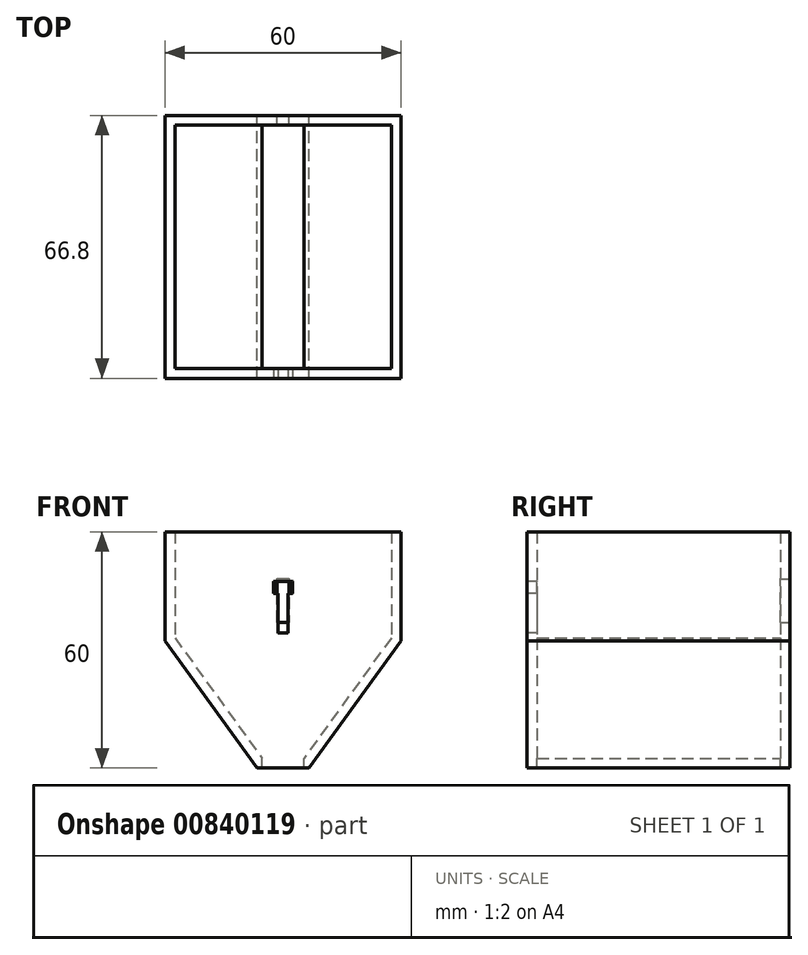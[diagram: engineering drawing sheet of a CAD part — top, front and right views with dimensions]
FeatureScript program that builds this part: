
annotation { "Feature Type Name" : "Feature", "Feature Type Description" : "" }
export const myFeature = defineFeature(function(context is Context, id is Id, definition is map)
    precondition{}
    {
        {
            var Q0;
            Q0=qCreatedBy(makeId("Front.planeOp"),FACE);
            var sketch = newSketch(context, id + "F0", { "sketchPlane" : qUnion([Q0])});
            skLineSegment(sketch, "E0", {"start": v(0, 4.02) * mm, "end": v(-30, 4.02) * mm});
            skLineSegment(sketch, "E1", {"start": v(-30, 4.02) * mm, "end": v(-30, -23.74) * mm});
            skLineSegment(sketch, "E2", {"start": v(-30, -23.74) * mm, "end": v(-6.6, -55.98) * mm});
            skLineSegment(sketch, "E3", {"start": v(-6.6, -55.98) * mm, "end": v(0, -55.98) * mm});
            skLineSegment(sketch, "E4", {"start": v(0, 4.02) * mm, "end": v(0, -55.98) * mm});
            skLineSegment(sketch, "E5.MirrorCS", {"start": v(0, 4.02) * mm, "end": v(30, 4.02) * mm});
            skLineSegment(sketch, "E6.MirrorCS", {"start": v(30, 4.02) * mm, "end": v(30, -23.74) * mm});
            skLineSegment(sketch, "E7.MirrorCS", {"start": v(30, -23.74) * mm, "end": v(6.6, -55.98) * mm});
            skLineSegment(sketch, "E8.MirrorCS", {"start": v(6.6, -55.98) * mm, "end": v(0, -55.98) * mm});
            skSolve(sketch);
        }
        {
            var Q0;
            Q0=makeQuery(id+"F0.imprint","IMPRINT",FACE,{"disambiguationData":[TD([[makeQuery(id+"F0.imprint","IMPRINT",EDGE,{"derivedFrom":sQuery(id+"F0.wireOp",EDGE,"E0")}),1.0]])]});
            var Q1;
            Q1=makeQuery(id+"F0.imprint","IMPRINT",FACE,{"disambiguationData":[TD([[makeQuery(id+"F0.imprint","IMPRINT",EDGE,{"derivedFrom":sQuery(id+"F0.wireOp",EDGE,"E4")}),1.0]])]});
            extrude(context, id + "F1", {"entities" : qUnion([Q0, Q1]), "depth" : 66.8 * mm, "offsetDistance" : 25 * mm});
        }
        {
            var Q0;
            Q0=makeQuery(id+"F1.opExtrude","SWEPT_FACE",FACE,{"disambiguationData":[OSD([sQuery(id+"F0.wireOp",EDGE,"E0"),sQuery(id+"F0.wireOp",EDGE,"E5.MirrorCS")])]});
            shell(context, id + "F2", {"entities" : qUnion([Q0]), "thickness" : 2.5 * mm});
        }
        {
            var Q0;
            Q0=makeQuery(id+"F2.opShell","OFFSET_FACE",FACE,{"disambiguationData":[OSD([sQuery(id+"F0.wireOp",EDGE,"E3"),sQuery(id+"F0.wireOp",EDGE,"E8.MirrorCS")])]});
            extrude(context, id + "F3", {"entities" : qUnion([Q0]), "operationType" : NewBodyOperationType.REMOVE, "oppositeDirection" : true, "depth" : 25 * mm, "offsetDistance" : 25 * mm});
        }
        {
            var Q0;
            Q0=makeQuery(id+"F1.opExtrude","CAP_FACE",FACE,{"disambiguationData":[OSD([sQuery(id+"F0.wireOp",EDGE,"E0"),sQuery(id+"F0.wireOp",EDGE,"E1"),sQuery(id+"F0.wireOp",EDGE,"E2"),sQuery(id+"F0.wireOp",EDGE,"E3"),sQuery(id+"F0.wireOp",EDGE,"E5.MirrorCS"),sQuery(id+"F0.wireOp",EDGE,"E6.MirrorCS"),sQuery(id+"F0.wireOp",EDGE,"E7.MirrorCS"),sQuery(id+"F0.wireOp",EDGE,"E8.MirrorCS")])],"isStart":false});
            var sketch = newSketch(context, id + "F4", { "sketchPlane" : qUnion([Q0])});
            skLineSegment(sketch, "E9", {"start": v(-2.4, -11.6) * mm, "end": v(-1.25, -11.6) * mm});
            skLineSegment(sketch, "E10", {"start": v(-1.25, -11.6) * mm, "end": v(-1.25, -21.6) * mm});
            skLineSegment(sketch, "E11", {"start": v(-1.25, -21.6) * mm, "end": v(0, -21.6) * mm});
            skLineSegment(sketch, "E12", {"start": v(-2.4, -11.6) * mm, "end": v(-2.4, -8.6) * mm});
            skLineSegment(sketch, "E13", {"start": v(-2.4, -8.6) * mm, "end": v(0, -8.6) * mm});
            skLineSegment(sketch, "E14", {"start": v(0, -8.6) * mm, "end": v(0, -21.6) * mm});
            skLineSegment(sketch, "E15.MirrorCS", {"start": v(2.4, -8.6) * mm, "end": v(0, -8.6) * mm});
            skLineSegment(sketch, "E16.MirrorCS", {"start": v(2.4, -11.6) * mm, "end": v(2.4, -8.6) * mm});
            skLineSegment(sketch, "E17.MirrorCS", {"start": v(2.4, -11.6) * mm, "end": v(1.25, -11.6) * mm});
            skLineSegment(sketch, "E18.MirrorCS", {"start": v(1.25, -11.6) * mm, "end": v(1.25, -21.6) * mm});
            skLineSegment(sketch, "E19.MirrorCS", {"start": v(1.25, -21.6) * mm, "end": v(0, -21.6) * mm});
            skSolve(sketch);
        }
        {
            var Q0;
            Q0=makeQuery(id+"F4.imprint","IMPRINT",FACE,{"disambiguationData":[TD([[makeQuery(id+"F4.imprint","IMPRINT",EDGE,{"derivedFrom":sQuery(id+"F4.wireOp",EDGE,"E9")}),1.0]])]});
            var Q1;
            Q1=makeQuery(id+"F4.imprint","IMPRINT",FACE,{"disambiguationData":[TD([[makeQuery(id+"F4.imprint","IMPRINT",EDGE,{"derivedFrom":sQuery(id+"F4.wireOp",EDGE,"E14")}),1.0]])]});
            extrude(context, id + "F5", {"entities" : qUnion([Q0, Q1]), "operationType" : NewBodyOperationType.REMOVE, "oppositeDirection" : true, "depth" : 25 * mm, "offsetDistance" : 25 * mm});
        }
        {
            var Q0;
            Q0=makeQuery(id+"F5.boolean.opBoolean","COPY",EDGE,{"derivedFrom":makeQuery(id+"F5.opExtrude","SWEPT_EDGE",EDGE,{"disambiguationData":[OSD([sQuery(id+"F4.wireOp",EDGE,"E17.MirrorCS"),sQuery(id+"F4.wireOp",EDGE,"E18.MirrorCS")])]})});
            var Q1;
            Q1=makeQuery(id+"F5.boolean.opBoolean","COPY",EDGE,{"derivedFrom":makeQuery(id+"F5.opExtrude","SWEPT_EDGE",EDGE,{"disambiguationData":[OSD([sQuery(id+"F4.wireOp",EDGE,"E9"),sQuery(id+"F4.wireOp",EDGE,"E10")])]})});
            var Q2;
            {var subQ0=sQuery(id+"F0.wireOp",EDGE,"E8.MirrorCS");var subQ1=sQuery(id+"F0.wireOp",EDGE,"E3");var subQ2=sQuery(id+"F0.wireOp",EDGE,"E7.MirrorCS");var subQ3=sQuery(id+"F0.wireOp",EDGE,"E6.MirrorCS");var subQ4=sQuery(id+"F0.wireOp",EDGE,"E5.MirrorCS");var subQ5=sQuery(id+"F0.wireOp",EDGE,"E2");var subQ6=sQuery(id+"F0.wireOp",EDGE,"E1");var subQ7=sQuery(id+"F0.wireOp",EDGE,"E0");Q2=makeQuery(id+"F5.boolean.opBoolean","INTERSECT",EDGE,{"derivedFrom":[makeQuery(id+"F3.boolean.opBoolean","MERGE",FACE,{"derivedFrom":[makeQuery(id+"F2.opShell","OFFSET_FACE",FACE,{"disambiguationData":[OSD([subQ7,subQ6,subQ5,subQ1,subQ4,subQ3,subQ2,subQ0]),TDD([makeQuery(id+"F1.opExtrude","CAP_FACE",FACE,{"disambiguationData":[OSD([subQ7,subQ6,subQ5,subQ1,subQ4,subQ3,subQ2,subQ0])],"isStart":false})])]}),makeQuery(id+"F3.opExtrude","SWEPT_FACE",FACE,{"disambiguationData":[OSD([subQ1,subQ0]),TDD([makeQuery(id+"F2.opShell","OFFSET_EDGE",EDGE,{"disambiguationData":[OSD([subQ1,subQ0]),TDD([makeQuery(id+"F1.opExtrude","CAP_EDGE",EDGE,{"disambiguationData":[OSD([subQ1,subQ0])],"isStart":false})])]})])]})]}),makeQuery(id+"F5.opExtrude","SWEPT_FACE",FACE,{"disambiguationData":[OSD([sQuery(id+"F4.wireOp",EDGE,"E13"),sQuery(id+"F4.wireOp",EDGE,"E15.MirrorCS")])]})]});}
            var Q3;
            {var subQ0=sQuery(id+"F0.wireOp",EDGE,"E8.MirrorCS");var subQ1=sQuery(id+"F0.wireOp",EDGE,"E3");var subQ2=sQuery(id+"F0.wireOp",EDGE,"E7.MirrorCS");var subQ3=sQuery(id+"F0.wireOp",EDGE,"E6.MirrorCS");var subQ4=sQuery(id+"F0.wireOp",EDGE,"E5.MirrorCS");var subQ5=sQuery(id+"F0.wireOp",EDGE,"E2");var subQ6=sQuery(id+"F0.wireOp",EDGE,"E1");var subQ7=sQuery(id+"F0.wireOp",EDGE,"E0");Q3=makeQuery(id+"F5.boolean.opBoolean","INTERSECT",EDGE,{"derivedFrom":[makeQuery(id+"F3.boolean.opBoolean","MERGE",FACE,{"derivedFrom":[makeQuery(id+"F2.opShell","OFFSET_FACE",FACE,{"disambiguationData":[OSD([subQ7,subQ6,subQ5,subQ1,subQ4,subQ3,subQ2,subQ0]),TDD([makeQuery(id+"F1.opExtrude","CAP_FACE",FACE,{"disambiguationData":[OSD([subQ7,subQ6,subQ5,subQ1,subQ4,subQ3,subQ2,subQ0])],"isStart":false})])]}),makeQuery(id+"F3.opExtrude","SWEPT_FACE",FACE,{"disambiguationData":[OSD([subQ1,subQ0]),TDD([makeQuery(id+"F2.opShell","OFFSET_EDGE",EDGE,{"disambiguationData":[OSD([subQ1,subQ0]),TDD([makeQuery(id+"F1.opExtrude","CAP_EDGE",EDGE,{"disambiguationData":[OSD([subQ1,subQ0])],"isStart":false})])]})])]})]}),makeQuery(id+"F5.opExtrude","SWEPT_FACE",FACE,{"disambiguationData":[OSD([sQuery(id+"F4.wireOp",EDGE,"E16.MirrorCS")])]})]});}
            var Q4;
            {var subQ0=sQuery(id+"F0.wireOp",EDGE,"E8.MirrorCS");var subQ1=sQuery(id+"F0.wireOp",EDGE,"E3");var subQ2=sQuery(id+"F0.wireOp",EDGE,"E7.MirrorCS");var subQ3=sQuery(id+"F0.wireOp",EDGE,"E6.MirrorCS");var subQ4=sQuery(id+"F0.wireOp",EDGE,"E5.MirrorCS");var subQ5=sQuery(id+"F0.wireOp",EDGE,"E2");var subQ6=sQuery(id+"F0.wireOp",EDGE,"E1");var subQ7=sQuery(id+"F0.wireOp",EDGE,"E0");Q4=makeQuery(id+"F5.boolean.opBoolean","INTERSECT",EDGE,{"derivedFrom":[makeQuery(id+"F3.boolean.opBoolean","MERGE",FACE,{"derivedFrom":[makeQuery(id+"F2.opShell","OFFSET_FACE",FACE,{"disambiguationData":[OSD([subQ7,subQ6,subQ5,subQ1,subQ4,subQ3,subQ2,subQ0]),TDD([makeQuery(id+"F1.opExtrude","CAP_FACE",FACE,{"disambiguationData":[OSD([subQ7,subQ6,subQ5,subQ1,subQ4,subQ3,subQ2,subQ0])],"isStart":false})])]}),makeQuery(id+"F3.opExtrude","SWEPT_FACE",FACE,{"disambiguationData":[OSD([subQ1,subQ0]),TDD([makeQuery(id+"F2.opShell","OFFSET_EDGE",EDGE,{"disambiguationData":[OSD([subQ1,subQ0]),TDD([makeQuery(id+"F1.opExtrude","CAP_EDGE",EDGE,{"disambiguationData":[OSD([subQ1,subQ0])],"isStart":false})])]})])]})]}),makeQuery(id+"F5.opExtrude","SWEPT_FACE",FACE,{"disambiguationData":[OSD([sQuery(id+"F4.wireOp",EDGE,"E17.MirrorCS")])]})]});}
            var Q5;
            {var subQ0=sQuery(id+"F0.wireOp",EDGE,"E8.MirrorCS");var subQ1=sQuery(id+"F0.wireOp",EDGE,"E3");var subQ2=sQuery(id+"F0.wireOp",EDGE,"E7.MirrorCS");var subQ3=sQuery(id+"F0.wireOp",EDGE,"E6.MirrorCS");var subQ4=sQuery(id+"F0.wireOp",EDGE,"E5.MirrorCS");var subQ5=sQuery(id+"F0.wireOp",EDGE,"E2");var subQ6=sQuery(id+"F0.wireOp",EDGE,"E1");var subQ7=sQuery(id+"F0.wireOp",EDGE,"E0");Q5=makeQuery(id+"F5.boolean.opBoolean","INTERSECT",EDGE,{"derivedFrom":[makeQuery(id+"F3.boolean.opBoolean","MERGE",FACE,{"derivedFrom":[makeQuery(id+"F2.opShell","OFFSET_FACE",FACE,{"disambiguationData":[OSD([subQ7,subQ6,subQ5,subQ1,subQ4,subQ3,subQ2,subQ0]),TDD([makeQuery(id+"F1.opExtrude","CAP_FACE",FACE,{"disambiguationData":[OSD([subQ7,subQ6,subQ5,subQ1,subQ4,subQ3,subQ2,subQ0])],"isStart":false})])]}),makeQuery(id+"F3.opExtrude","SWEPT_FACE",FACE,{"disambiguationData":[OSD([subQ1,subQ0]),TDD([makeQuery(id+"F2.opShell","OFFSET_EDGE",EDGE,{"disambiguationData":[OSD([subQ1,subQ0]),TDD([makeQuery(id+"F1.opExtrude","CAP_EDGE",EDGE,{"disambiguationData":[OSD([subQ1,subQ0])],"isStart":false})])]})])]})]}),makeQuery(id+"F5.opExtrude","SWEPT_FACE",FACE,{"disambiguationData":[OSD([sQuery(id+"F4.wireOp",EDGE,"E18.MirrorCS")])]})]});}
            var Q6;
            {var subQ0=sQuery(id+"F0.wireOp",EDGE,"E8.MirrorCS");var subQ1=sQuery(id+"F0.wireOp",EDGE,"E3");var subQ2=sQuery(id+"F0.wireOp",EDGE,"E7.MirrorCS");var subQ3=sQuery(id+"F0.wireOp",EDGE,"E6.MirrorCS");var subQ4=sQuery(id+"F0.wireOp",EDGE,"E5.MirrorCS");var subQ5=sQuery(id+"F0.wireOp",EDGE,"E2");var subQ6=sQuery(id+"F0.wireOp",EDGE,"E1");var subQ7=sQuery(id+"F0.wireOp",EDGE,"E0");Q6=makeQuery(id+"F5.boolean.opBoolean","INTERSECT",EDGE,{"derivedFrom":[makeQuery(id+"F3.boolean.opBoolean","MERGE",FACE,{"derivedFrom":[makeQuery(id+"F2.opShell","OFFSET_FACE",FACE,{"disambiguationData":[OSD([subQ7,subQ6,subQ5,subQ1,subQ4,subQ3,subQ2,subQ0]),TDD([makeQuery(id+"F1.opExtrude","CAP_FACE",FACE,{"disambiguationData":[OSD([subQ7,subQ6,subQ5,subQ1,subQ4,subQ3,subQ2,subQ0])],"isStart":false})])]}),makeQuery(id+"F3.opExtrude","SWEPT_FACE",FACE,{"disambiguationData":[OSD([subQ1,subQ0]),TDD([makeQuery(id+"F2.opShell","OFFSET_EDGE",EDGE,{"disambiguationData":[OSD([subQ1,subQ0]),TDD([makeQuery(id+"F1.opExtrude","CAP_EDGE",EDGE,{"disambiguationData":[OSD([subQ1,subQ0])],"isStart":false})])]})])]})]}),makeQuery(id+"F5.opExtrude","SWEPT_FACE",FACE,{"disambiguationData":[OSD([sQuery(id+"F4.wireOp",EDGE,"E12")])]})]});}
            var Q7;
            {var subQ0=sQuery(id+"F0.wireOp",EDGE,"E8.MirrorCS");var subQ1=sQuery(id+"F0.wireOp",EDGE,"E3");var subQ2=sQuery(id+"F0.wireOp",EDGE,"E7.MirrorCS");var subQ3=sQuery(id+"F0.wireOp",EDGE,"E6.MirrorCS");var subQ4=sQuery(id+"F0.wireOp",EDGE,"E5.MirrorCS");var subQ5=sQuery(id+"F0.wireOp",EDGE,"E2");var subQ6=sQuery(id+"F0.wireOp",EDGE,"E1");var subQ7=sQuery(id+"F0.wireOp",EDGE,"E0");Q7=makeQuery(id+"F5.boolean.opBoolean","INTERSECT",EDGE,{"derivedFrom":[makeQuery(id+"F3.boolean.opBoolean","MERGE",FACE,{"derivedFrom":[makeQuery(id+"F2.opShell","OFFSET_FACE",FACE,{"disambiguationData":[OSD([subQ7,subQ6,subQ5,subQ1,subQ4,subQ3,subQ2,subQ0]),TDD([makeQuery(id+"F1.opExtrude","CAP_FACE",FACE,{"disambiguationData":[OSD([subQ7,subQ6,subQ5,subQ1,subQ4,subQ3,subQ2,subQ0])],"isStart":false})])]}),makeQuery(id+"F3.opExtrude","SWEPT_FACE",FACE,{"disambiguationData":[OSD([subQ1,subQ0]),TDD([makeQuery(id+"F2.opShell","OFFSET_EDGE",EDGE,{"disambiguationData":[OSD([subQ1,subQ0]),TDD([makeQuery(id+"F1.opExtrude","CAP_EDGE",EDGE,{"disambiguationData":[OSD([subQ1,subQ0])],"isStart":false})])]})])]})]}),makeQuery(id+"F5.opExtrude","SWEPT_FACE",FACE,{"disambiguationData":[OSD([sQuery(id+"F4.wireOp",EDGE,"E9")])]})]});}
            var Q8;
            {var subQ0=sQuery(id+"F0.wireOp",EDGE,"E8.MirrorCS");var subQ1=sQuery(id+"F0.wireOp",EDGE,"E3");var subQ2=sQuery(id+"F0.wireOp",EDGE,"E7.MirrorCS");var subQ3=sQuery(id+"F0.wireOp",EDGE,"E6.MirrorCS");var subQ4=sQuery(id+"F0.wireOp",EDGE,"E5.MirrorCS");var subQ5=sQuery(id+"F0.wireOp",EDGE,"E2");var subQ6=sQuery(id+"F0.wireOp",EDGE,"E1");var subQ7=sQuery(id+"F0.wireOp",EDGE,"E0");Q8=makeQuery(id+"F5.boolean.opBoolean","INTERSECT",EDGE,{"derivedFrom":[makeQuery(id+"F3.boolean.opBoolean","MERGE",FACE,{"derivedFrom":[makeQuery(id+"F2.opShell","OFFSET_FACE",FACE,{"disambiguationData":[OSD([subQ7,subQ6,subQ5,subQ1,subQ4,subQ3,subQ2,subQ0]),TDD([makeQuery(id+"F1.opExtrude","CAP_FACE",FACE,{"disambiguationData":[OSD([subQ7,subQ6,subQ5,subQ1,subQ4,subQ3,subQ2,subQ0])],"isStart":false})])]}),makeQuery(id+"F3.opExtrude","SWEPT_FACE",FACE,{"disambiguationData":[OSD([subQ1,subQ0]),TDD([makeQuery(id+"F2.opShell","OFFSET_EDGE",EDGE,{"disambiguationData":[OSD([subQ1,subQ0]),TDD([makeQuery(id+"F1.opExtrude","CAP_EDGE",EDGE,{"disambiguationData":[OSD([subQ1,subQ0])],"isStart":false})])]})])]})]}),makeQuery(id+"F5.opExtrude","SWEPT_FACE",FACE,{"disambiguationData":[OSD([sQuery(id+"F4.wireOp",EDGE,"E11"),sQuery(id+"F4.wireOp",EDGE,"E19.MirrorCS")])]})]});}
            var Q9;
            {var subQ0=sQuery(id+"F0.wireOp",EDGE,"E8.MirrorCS");var subQ1=sQuery(id+"F0.wireOp",EDGE,"E3");var subQ2=sQuery(id+"F0.wireOp",EDGE,"E7.MirrorCS");var subQ3=sQuery(id+"F0.wireOp",EDGE,"E6.MirrorCS");var subQ4=sQuery(id+"F0.wireOp",EDGE,"E5.MirrorCS");var subQ5=sQuery(id+"F0.wireOp",EDGE,"E2");var subQ6=sQuery(id+"F0.wireOp",EDGE,"E1");var subQ7=sQuery(id+"F0.wireOp",EDGE,"E0");Q9=makeQuery(id+"F5.boolean.opBoolean","INTERSECT",EDGE,{"derivedFrom":[makeQuery(id+"F3.boolean.opBoolean","MERGE",FACE,{"derivedFrom":[makeQuery(id+"F2.opShell","OFFSET_FACE",FACE,{"disambiguationData":[OSD([subQ7,subQ6,subQ5,subQ1,subQ4,subQ3,subQ2,subQ0]),TDD([makeQuery(id+"F1.opExtrude","CAP_FACE",FACE,{"disambiguationData":[OSD([subQ7,subQ6,subQ5,subQ1,subQ4,subQ3,subQ2,subQ0])],"isStart":false})])]}),makeQuery(id+"F3.opExtrude","SWEPT_FACE",FACE,{"disambiguationData":[OSD([subQ1,subQ0]),TDD([makeQuery(id+"F2.opShell","OFFSET_EDGE",EDGE,{"disambiguationData":[OSD([subQ1,subQ0]),TDD([makeQuery(id+"F1.opExtrude","CAP_EDGE",EDGE,{"disambiguationData":[OSD([subQ1,subQ0])],"isStart":false})])]})])]})]}),makeQuery(id+"F5.opExtrude","SWEPT_FACE",FACE,{"disambiguationData":[OSD([sQuery(id+"F4.wireOp",EDGE,"E10")])]})]});}
            fillet(context, id + "F6", {"entities" : qUnion([Q0, Q1, Q2, Q3, Q4, Q5, Q6, Q7, Q8, Q9]), "radius" : 0.2 * mm, "tangentPropagation" : true, "allowEdgeOverflow" : false});
        }
        {
            var Q0;
            Q0=makeQuery(id+"F1.opExtrude","CAP_FACE",FACE,{"disambiguationData":[OSD([sQuery(id+"F0.wireOp",EDGE,"E0"),sQuery(id+"F0.wireOp",EDGE,"E1"),sQuery(id+"F0.wireOp",EDGE,"E2"),sQuery(id+"F0.wireOp",EDGE,"E3"),sQuery(id+"F0.wireOp",EDGE,"E5.MirrorCS"),sQuery(id+"F0.wireOp",EDGE,"E6.MirrorCS"),sQuery(id+"F0.wireOp",EDGE,"E7.MirrorCS"),sQuery(id+"F0.wireOp",EDGE,"E8.MirrorCS")])],"isStart":true});
            var sketch = newSketch(context, id + "F7", { "sketchPlane" : qUnion([Q0])});
            skLineSegment(sketch, "E20", {"start": v(0, -7.98) * mm, "end": v(-1.5, -7.98) * mm});
            skLineSegment(sketch, "E21", {"start": v(-1.5, -7.98) * mm, "end": v(-1.5, -18.98) * mm});
            skLineSegment(sketch, "E22", {"start": v(-1.5, -18.98) * mm, "end": v(0, -18.98) * mm});
            skLineSegment(sketch, "E23.MirrorCS", {"start": v(0, -7.98) * mm, "end": v(1.5, -7.98) * mm});
            skLineSegment(sketch, "E24.MirrorCS", {"start": v(1.5, -7.98) * mm, "end": v(1.5, -18.98) * mm});
            skLineSegment(sketch, "E25.MirrorCS", {"start": v(1.5, -18.98) * mm, "end": v(0, -18.98) * mm});
            skSolve(sketch);
        }
        {
            var Q0;
            Q0=makeQuery(id+"F7.imprint","IMPRINT",FACE,{"disambiguationData":[TD([[makeQuery(id+"F7.imprint","IMPRINT",EDGE,{"derivedFrom":sQuery(id+"F7.wireOp",EDGE,"E20")}),1.0]])]});
            extrude(context, id + "F8", {"entities" : qUnion([Q0]), "operationType" : NewBodyOperationType.REMOVE, "oppositeDirection" : true, "depth" : 25 * mm, "offsetDistance" : 25 * mm});
        }
        {
            var Q0;
            {var subQ0=sQuery(id+"F0.wireOp",EDGE,"E8.MirrorCS");var subQ1=sQuery(id+"F0.wireOp",EDGE,"E3");var subQ2=sQuery(id+"F0.wireOp",EDGE,"E7.MirrorCS");var subQ3=sQuery(id+"F0.wireOp",EDGE,"E6.MirrorCS");var subQ4=sQuery(id+"F0.wireOp",EDGE,"E5.MirrorCS");var subQ5=sQuery(id+"F0.wireOp",EDGE,"E2");var subQ6=sQuery(id+"F0.wireOp",EDGE,"E1");var subQ7=sQuery(id+"F0.wireOp",EDGE,"E0");Q0=makeQuery(id+"F8.boolean.opBoolean","INTERSECT",EDGE,{"derivedFrom":[makeQuery(id+"F3.boolean.opBoolean","MERGE",FACE,{"derivedFrom":[makeQuery(id+"F2.opShell","OFFSET_FACE",FACE,{"disambiguationData":[OSD([subQ7,subQ6,subQ5,subQ1,subQ4,subQ3,subQ2,subQ0]),TDD([makeQuery(id+"F1.opExtrude","CAP_FACE",FACE,{"disambiguationData":[OSD([subQ7,subQ6,subQ5,subQ1,subQ4,subQ3,subQ2,subQ0])],"isStart":true})])]}),makeQuery(id+"F3.opExtrude","SWEPT_FACE",FACE,{"disambiguationData":[OSD([subQ1,subQ0]),TDD([makeQuery(id+"F2.opShell","OFFSET_EDGE",EDGE,{"disambiguationData":[OSD([subQ1,subQ0]),TDD([makeQuery(id+"F1.opExtrude","CAP_EDGE",EDGE,{"disambiguationData":[OSD([subQ1,subQ0])],"isStart":true})])]})])]})]}),makeQuery(id+"F8.opExtrude","SWEPT_FACE",FACE,{"disambiguationData":[OSD([sQuery(id+"F7.wireOp",EDGE,"E20"),sQuery(id+"F7.wireOp",EDGE,"E23.MirrorCS")])]})]});}
            fillet(context, id + "F9", {"entities" : qUnion([Q0]), "radius" : 0.2 * mm, "tangentPropagation" : true, "allowEdgeOverflow" : false});
        }
    });
